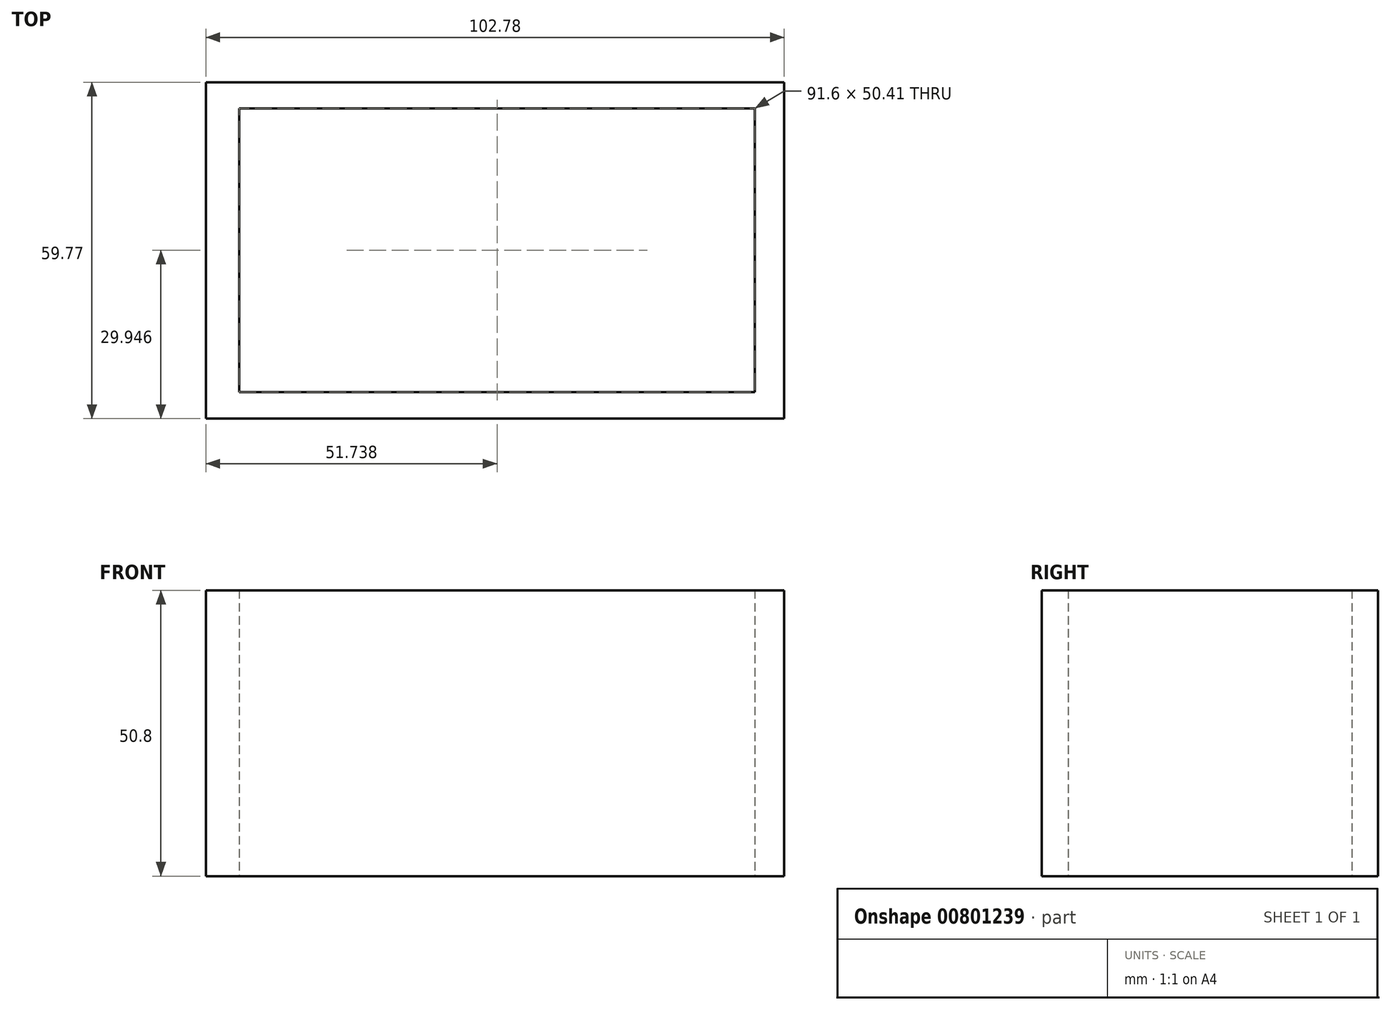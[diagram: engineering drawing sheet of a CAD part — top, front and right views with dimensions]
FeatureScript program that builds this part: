
annotation { "Feature Type Name" : "Feature", "Feature Type Description" : "" }
export const myFeature = defineFeature(function(context is Context, id is Id, definition is map)
    precondition{}
    {
        {
            var Q0;
            Q0=qCreatedBy(makeId("Top.planeOp"),FACE);
            var sketch = newSketch(context, id + "F0", { "sketchPlane" : qUnion([Q0])});
            skLineSegment(sketch, "E0.bottom", {"start": v(0, 0) * mm, "end": v(102.78, 0) * mm});
            skLineSegment(sketch, "E0.top", {"start": v(0, 59.77) * mm, "end": v(102.78, 59.77) * mm});
            skLineSegment(sketch, "E0.left", {"start": v(0, 0) * mm, "end": v(0, 59.77) * mm});
            skLineSegment(sketch, "E0.right", {"start": v(102.78, 0) * mm, "end": v(102.78, 59.77) * mm});
            skLineSegment(sketch, "E1.bottom", {"start": v(5.94, 4.74) * mm, "end": v(97.54, 4.74) * mm});
            skLineSegment(sketch, "E1.top", {"start": v(5.94, 55.15) * mm, "end": v(97.54, 55.15) * mm});
            skLineSegment(sketch, "E1.left", {"start": v(5.94, 4.74) * mm, "end": v(5.94, 55.15) * mm});
            skLineSegment(sketch, "E1.right", {"start": v(97.54, 4.74) * mm, "end": v(97.54, 55.15) * mm});
            skSolve(sketch);
        }
        {
            var Q0;
            Q0=makeQuery(id+"F0.imprint","IMPRINT",FACE,{"disambiguationData":[TD([[makeQuery(id+"F0.imprint","IMPRINT",EDGE,{"derivedFrom":sQuery(id+"F0.wireOp",EDGE,"E0.bottom")}),1.0]])]});
            extrude(context, id + "F1", {"entities" : qUnion([Q0]), "depth" : 25.4 * mm, "offsetDistance" : 25.4 * mm});
        }
        {
            var Q0;
            Q0=makeQuery(id+"F1.opExtrude","CAP_FACE",FACE,{"disambiguationData":[OSD([sQuery(id+"F0.wireOp",EDGE,"E0.bottom"),sQuery(id+"F0.wireOp",EDGE,"E0.top"),sQuery(id+"F0.wireOp",EDGE,"E0.left"),sQuery(id+"F0.wireOp",EDGE,"E0.right"),sQuery(id+"F0.wireOp",EDGE,"E1.bottom"),sQuery(id+"F0.wireOp",EDGE,"E1.top"),sQuery(id+"F0.wireOp",EDGE,"E1.left"),sQuery(id+"F0.wireOp",EDGE,"E1.right")])],"isStart":false});
            extrude(context, id + "F2", {"entities" : qUnion([Q0]), "operationType" : NewBodyOperationType.ADD, "depth" : 25.4 * mm, "offsetDistance" : 25.4 * mm});
        }
    });
